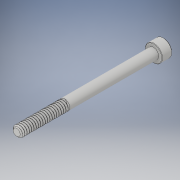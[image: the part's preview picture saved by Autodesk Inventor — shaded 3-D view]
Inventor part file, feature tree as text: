
AUTODESK INVENTOR PART (.ipt)
format: ipt  version: 2018 (Build 220112000, 112)  size: 741,888 bytes
history: native  units: in
note: dims shown in document units (in); Inventor stores cm internally (conversion verified against a paired STEP export)
features: chamfer x1
ambient origin geometry x8: Origin, YZ Plane, XZ Plane, XY Plane, X Axis, Y Axis, Z Axis, Center Point
bodies: Solid1 (feature_tree)
feature tree (1):
  chamfer  "Chamfer2"  [1 undecoded]
note: 1 required parameter value undecoded (feature->parameter linkage not recoverable at this tier; creation-order binding heuristic only, values carry confidence <= 0.55)
